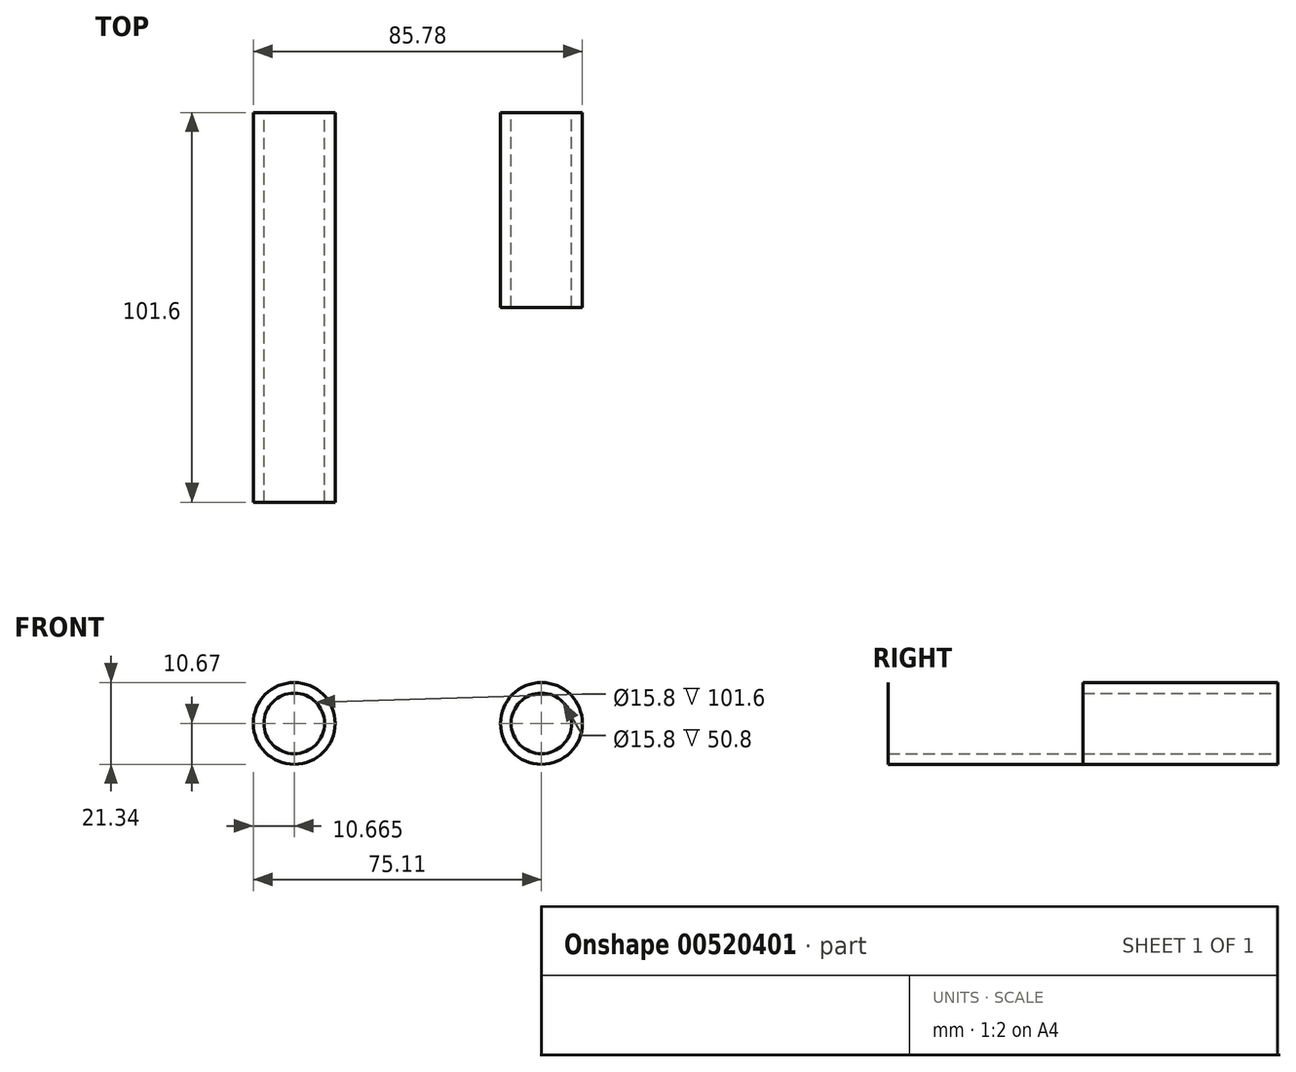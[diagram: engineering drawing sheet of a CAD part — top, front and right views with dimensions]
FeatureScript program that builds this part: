
annotation { "Feature Type Name" : "Feature", "Feature Type Description" : "" }
export const myFeature = defineFeature(function(context is Context, id is Id, definition is map)
    precondition{}
    {
        {
            var Q0;
            Q0=qCreatedBy(makeId("Front.planeOp"),FACE);
            var sketch = newSketch(context, id + "F0", { "sketchPlane" : qUnion([Q0])});
            skCircle(sketch, "E0", {"center": v(0, 0) * mm, "radius": 7.9 * mm});
            skCircle(sketch, "E1", {"center": v(0, 0) * mm, "radius": 10.67 * mm});
            skSolve(sketch);
        }
        {
            var Q0;
            Q0=makeQuery(id+"F0.imprint","IMPRINT",FACE,{"disambiguationData":[TD([[makeQuery(id+"F0.imprint","IMPRINT",EDGE,{"derivedFrom":sQuery(id+"F0.wireOp",EDGE,"E0")}),-1.0]])]});
            extrude(context, id + "F1", {"entities" : qUnion([Q0]), "depth" : 50.8 * mm, "offsetDistance" : 25.4 * mm});
        }
        {
            var Q0;
            Q0=qCreatedBy(makeId("Front.planeOp"),FACE);
            var sketch = newSketch(context, id + "F2", { "sketchPlane" : qUnion([Q0])});
            skCircle(sketch, "E2", {"center": v(-64.45, 0) * mm, "radius": 10.67 * mm});
            skCircle(sketch, "E3", {"center": v(-64.45, 0) * mm, "radius": 7.9 * mm});
            skSolve(sketch);
        }
        {
            var Q0;
            Q0=makeQuery(id+"F2.imprint","IMPRINT",FACE,{"disambiguationData":[TD([[makeQuery(id+"F2.imprint","IMPRINT",EDGE,{"derivedFrom":sQuery(id+"F2.wireOp",EDGE,"E2")}),1.0]])]});
            extrude(context, id + "F3", {"entities" : qUnion([Q0]), "depth" : 101.6 * mm, "offsetDistance" : 25.4 * mm});
        }
    });
